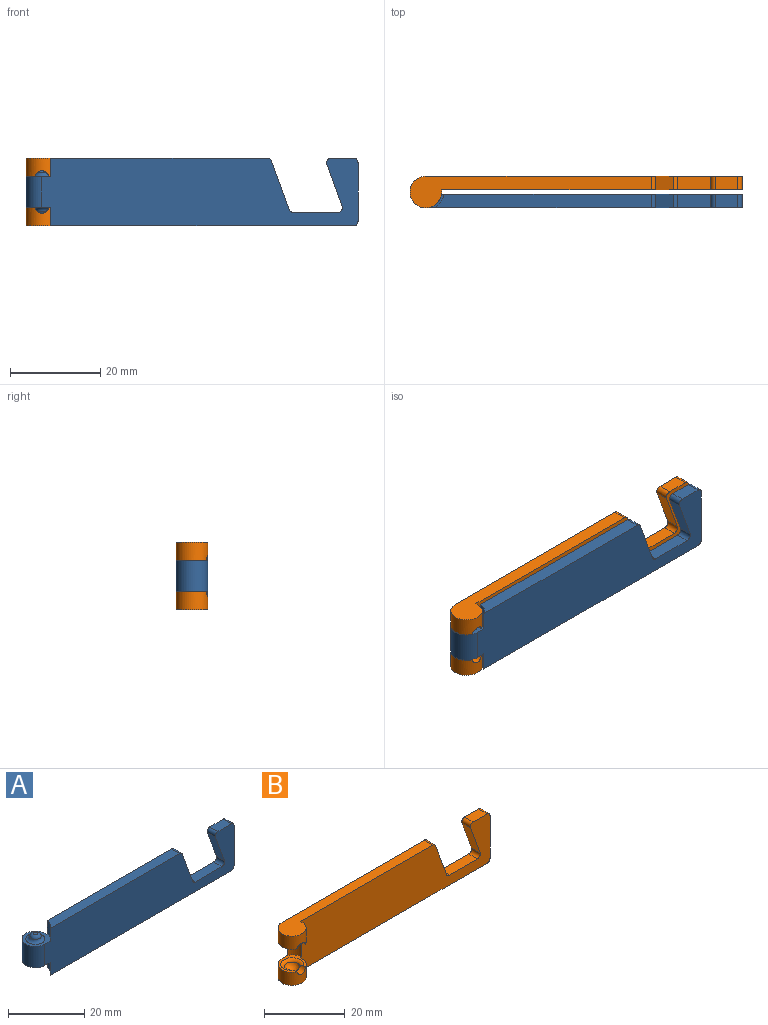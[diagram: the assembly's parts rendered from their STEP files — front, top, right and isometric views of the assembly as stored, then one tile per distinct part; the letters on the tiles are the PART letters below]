
ASSEMBLY  parts=2 mates=1
PART A: 26 faces, bbox 73.5x7x15 mm
  f0: plane 48x3mm, normal (0,0,1), area 139.9mm2, adj f1,f2,f12,f22
  f1: plane 66.54x15mm, normal (0,1,0), area 849.5mm2, adj f0,f3,f4,f5,f6,f7,f11,f12
  f2: plane 70x15mm, normal (0,-1,0), area 889.7mm2, adj f0,f3,f4,f5,f6,f7,f11,f12
  f3: plane 67.06x3mm, normal (0,0,-1), area 197.1mm2, adj f1,f2,f5,f25
  f4: plane 13x3mm, normal (1,0,0), area 39mm2, adj f1,f2,f24,f25
  f5: cylinder r=4mm len=4.1mm, axis (0,0,1), area 15.4mm2, adj f1,f2,f3,f6
  f6: plane 7.47x7mm, normal (0,0,-1), area 20.9mm2, adj f1,f2,f5,f7,f9
  f7: cylinder r=3.5mm len=7mm, axis (0,0,1), area 115.6mm2, adj f1,f2,f6,f13
  f8: plane 1.05x1.05mm, normal (0,0,-1), area 0.9mm2, adj f10
  f9: torus R=2.5mm, axis (0,0,-1), area 17mm2, adj f6,f10
  f10: torus R=0.52mm, axis (0,0,1), area 10mm2, adj f8,f9
  f11: plane 4.94x3mm, normal (0,0,1), area 14.8mm2, adj f1,f2,f23,f24
  f12: cylinder r=4mm len=4.1mm, axis (0,0,-1), area 15.4mm2, adj f0,f1,f2,f13
  f13: plane 7.47x7mm, normal (0,0,1), area 20.9mm2, adj f1,f2,f7,f12,f15
  f14: plane 1.05x1.05mm, normal (0,0,1), area 0.9mm2, adj f16
  f15: torus R=2.5mm, axis (0,0,1), area 17mm2, adj f13,f16
  f16: torus R=0.52mm, axis (0,0,-1), area 10mm2, adj f14,f15
  f17: plane 9.32x3.39mm, normal (-0.94,0,-0.34), area 29.7mm2, adj f1,f2,f21,f23
  f18: plane 10.68x3.89mm, normal (0.94,0,0.34), area 34.1mm2, adj f1,f2,f20,f22
  f19: plane 9.87x3mm, normal (0,0,1), area 29.6mm2, adj f1,f2,f20,f21
  f20: cylinder r=1mm len=3mm, axis (0,1,0), area 3.7mm2, adj f1,f2,f18,f19
  f21: cylinder r=1mm len=3mm, axis (0,1,0), area 5.8mm2, adj f1,f2,f17,f19
  f22: cylinder r=1mm len=3mm, axis (0,1,0), area 3.7mm2, adj f0,f1,f2,f18
  f23: cylinder r=1mm len=3mm, axis (0,1,0), area 5.8mm2, adj f1,f2,f11,f17
  f24: cylinder r=1mm len=3mm, axis (0,-1,0), area 4.7mm2, adj f1,f2,f4,f11
  f25: cylinder r=1mm len=3mm, axis (0,-1,0), area 4.7mm2, adj f1,f2,f3,f4
PART B: 30 faces, bbox 73.8x7.3x15 mm
  f0: plane 66.54x15mm, normal (0,-1,0), area 850.1mm2, adj f2,f4,f5,f6,f7,f8,f14,f15
  f1: plane 70x15mm, normal (0,1,0), area 892mm2, adj f2,f4,f5,f6,f7,f8,f14,f15
  f2: plane 53.43x7mm, normal (0,0,1), area 180.4mm2, adj f0,f1,f14,f25
  f3: plane 0.2x0.15mm, normal (0,-1,0), area 0mm2, adj f9,f11,f12
  f4: cylinder r=3.5mm len=7mm, axis (0,0,-1), area 65.3mm2, adj f0,f1,f5,f6,f9
  f5: plane 7.47x6.68mm, normal (0,0,1), area 13.3mm2, adj f0,f1,f4,f8,f9,f12
  f6: plane 72.5x7mm, normal (0,0,-1), area 237.6mm2, adj f0,f1,f4,f29
  f7: plane 13x3mm, normal (1,0,0), area 39mm2, adj f0,f1,f28,f29
  f8: cylinder r=4mm len=7mm, axis (0,0,-1), area 26.3mm2, adj f0,f1,f5,f15
  f9: cylinder r=1.5mm len=2.94mm, axis (0,1,0), area 7.2mm2, adj f3,f4,f5,f10,f11,f12
  f10: plane 0.2x0.15mm, normal (0,-1,0), area 0mm2, adj f9,f11,f12
  f11: sphere r=2mm, area 15.8mm2, adj f3,f9,f10,f12
  f12: torus R=2.83mm, axis (0,0,1), area 14mm2, adj f3,f5,f9,f10,f11
  f13: plane 0.2x0.15mm, normal (0,-1,0), area 0mm2, adj f17,f19,f20
  f14: cylinder r=3.5mm len=7mm, axis (0,0,1), area 65.3mm2, adj f0,f1,f2,f15,f17
  f15: plane 7.47x6.68mm, normal (0,0,-1), area 13.3mm2, adj f0,f1,f8,f14,f17,f20
  f16: plane 4.94x3mm, normal (0,0,1), area 14.8mm2, adj f0,f1,f24,f28
  f17: cylinder r=1.5mm len=2.94mm, axis (0,1,0), area 7.2mm2, adj f13,f14,f15,f18,f19,f20
  f18: plane 0.2x0.15mm, normal (0,-1,0), area 0mm2, adj f17,f19,f20
  f19: sphere r=2mm, area 15.8mm2, adj f13,f17,f18,f20
  f20: torus R=2.83mm, axis (0,0,-1), area 14mm2, adj f13,f15,f17,f18,f19
  f21: plane 9.87x3mm, normal (0,0,1), area 29.6mm2, adj f0,f1,f26,f27
  f22: plane 9.32x3.39mm, normal (-0.94,0,-0.34), area 29.7mm2, adj f0,f1,f24,f27
  f23: plane 10.68x3.89mm, normal (0.94,0,0.34), area 34.1mm2, adj f0,f1,f25,f26
  f24: cylinder r=1mm len=3mm, axis (0,1,0), area 5.8mm2, adj f0,f1,f16,f22
  f25: cylinder r=1mm len=3mm, axis (0,1,0), area 3.7mm2, adj f0,f1,f2,f23
  f26: cylinder r=1mm len=3mm, axis (0,1,0), area 3.7mm2, adj f0,f1,f21,f23
  f27: cylinder r=1mm len=3mm, axis (0,1,0), area 5.8mm2, adj f0,f1,f21,f22
  f28: cylinder r=1mm len=3mm, axis (0,1,0), area 4.7mm2, adj f0,f1,f7,f16
  f29: cylinder r=1mm len=3mm, axis (0,1,0), area 4.7mm2, adj f0,f1,f6,f7
PLACE A t=(52.32,19.54,-1.45)mm
PLACE B t=(52.32,10.54,-1.45)mm
MATE revolute A.f5 <-> B.f4  axis (0,0,1) through (17.32,7.04,6.05)mm
